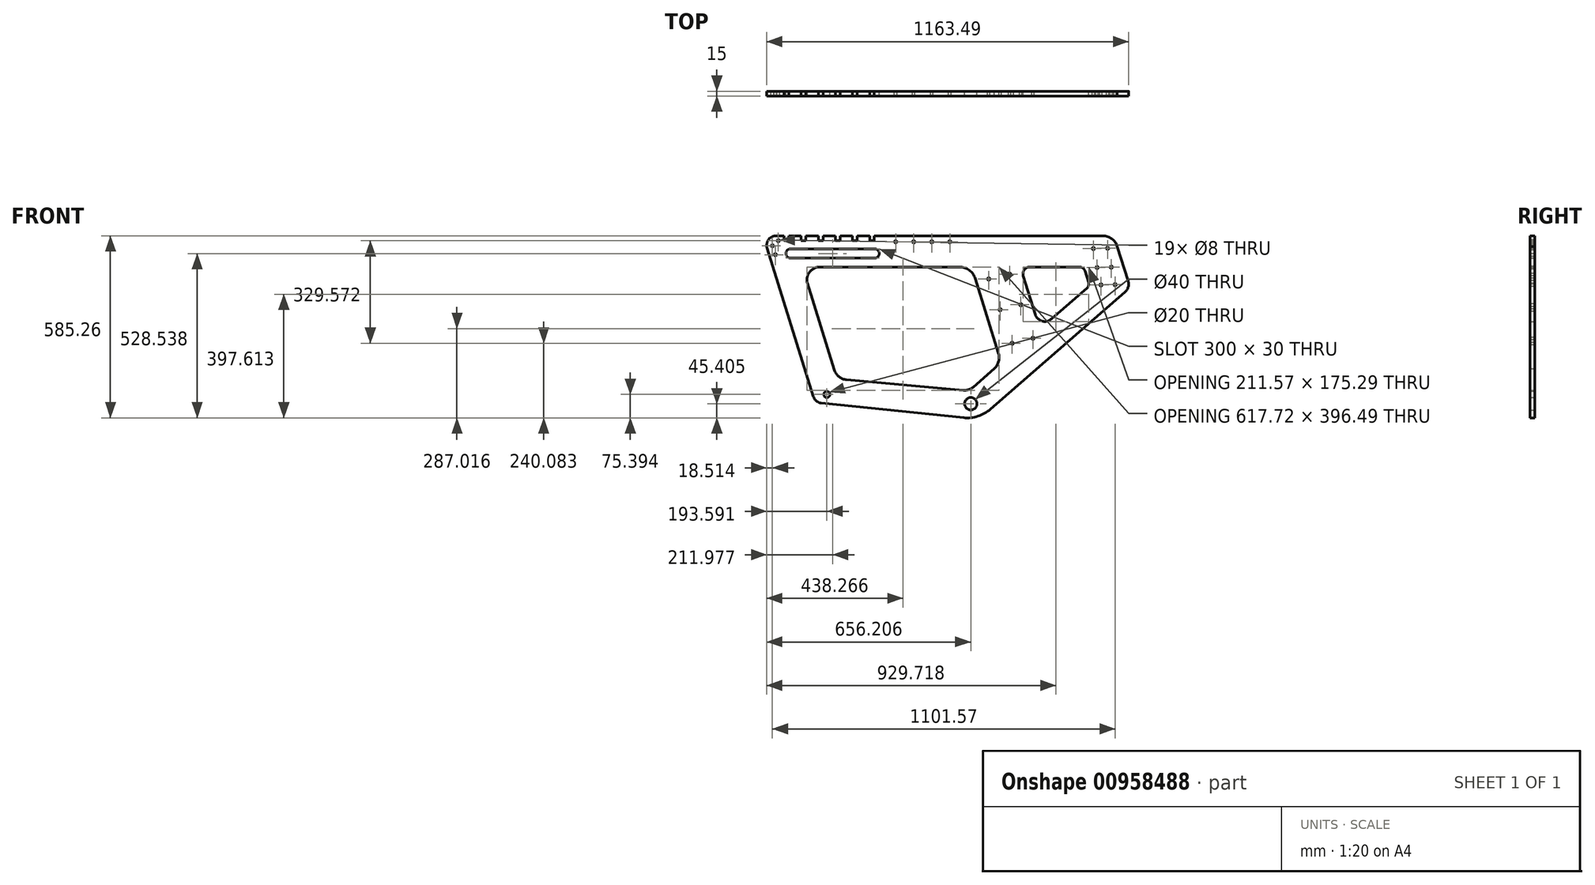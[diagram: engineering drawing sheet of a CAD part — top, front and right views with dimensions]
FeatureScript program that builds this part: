
annotation { "Feature Type Name" : "Feature", "Feature Type Description" : "" }
export const myFeature = defineFeature(function(context is Context, id is Id, definition is map)
    precondition{}
    {
        {
            var Q0;
            Q0=qCreatedBy(makeId("Front.planeOp"),FACE);
            var sketch = newSketch(context, id + "F0", { "sketchPlane" : qUnion([Q0])});
            skLineSegment(sketch, "E0", {"start": v(-250.21, -41.28) * mm, "end": v(207.37, -88.34) * mm});
            skLineSegment(sketch, "E1", {"start": v(-424.46, 456.77) * mm, "end": v(-275.56, -20.55) * mm});
            skLineSegment(sketch, "E2", {"start": v(293.18, -61.15) * mm, "end": v(726.16, 315.74) * mm});
            skArc(sketch, "E3", {"start": v(-275.56, -20.55) * mm, "mid": v(-266, -34.72) * mm, "end": v(-250.21, -41.28) * mm});
            skLineSegment(sketch, "E4", {"start": v(-295.43, 345.38) * mm, "end": v(-208.05, 65.27) * mm});
            skLineSegment(sketch, "E5", {"start": v(238.22, 10.33) * mm, "end": v(306.1, 69.42) * mm});
            skLineSegment(sketch, "E6", {"start": v(701.38, 462.39) * mm, "end": v(736.13, 350.96) * mm});
            skArc(sketch, "E7", {"start": v(207.37, -88.34) * mm, "mid": v(253.1, -83.65) * mm, "end": v(293.18, -61.15) * mm});
            skLineSegment(sketch, "E8", {"start": v(-254.58, 396.32) * mm, "end": v(193.57, 396.32) * mm});
            skLineSegment(sketch, "E9.bottom", {"start": v(-369.7, 496.32) * mm, "end": v(-354.7, 496.32) * mm});
            skLineSegment(sketch, "E9.top", {"start": v(-369.7, 481.32) * mm, "end": v(-354.7, 481.32) * mm});
            skLineSegment(sketch, "E9.left", {"start": v(-369.7, 496.32) * mm, "end": v(-369.7, 481.32) * mm});
            skLineSegment(sketch, "E9.right", {"start": v(-354.7, 496.32) * mm, "end": v(-354.7, 481.32) * mm});
            skLineSegment(sketch, "E10.bottom", {"start": v(-348.86, 454.6) * mm, "end": v(-78.86, 454.6) * mm});
            skLineSegment(sketch, "E10.top", {"start": v(-348.86, 424.6) * mm, "end": v(-78.86, 424.6) * mm});
            skArc(sketch, "E11", {"start": v(-78.86, 424.6) * mm, "mid": v(-63.86, 439.6) * mm, "end": v(-78.86, 454.6) * mm});
            skArc(sketch, "E12", {"start": v(-348.86, 454.6) * mm, "mid": v(-363.86, 439.6) * mm, "end": v(-348.86, 424.6) * mm});
            skLineSegment(sketch, "E13.bottom", {"start": v(-314.7, 496.32) * mm, "end": v(-299.7, 496.32) * mm});
            skLineSegment(sketch, "E13.top", {"start": v(-314.7, 481.32) * mm, "end": v(-299.7, 481.32) * mm});
            skLineSegment(sketch, "E13.left", {"start": v(-314.7, 496.32) * mm, "end": v(-314.7, 481.32) * mm});
            skLineSegment(sketch, "E13.right", {"start": v(-299.7, 496.32) * mm, "end": v(-299.7, 481.32) * mm});
            skLineSegment(sketch, "E14.bottom", {"start": v(-259.7, 496.32) * mm, "end": v(-244.7, 496.32) * mm});
            skLineSegment(sketch, "E14.top", {"start": v(-259.7, 481.32) * mm, "end": v(-244.7, 481.32) * mm});
            skLineSegment(sketch, "E14.left", {"start": v(-259.7, 496.32) * mm, "end": v(-259.7, 481.32) * mm});
            skLineSegment(sketch, "E14.right", {"start": v(-244.7, 496.32) * mm, "end": v(-244.7, 481.32) * mm});
            skLineSegment(sketch, "E15.bottom", {"start": v(-204.7, 496.32) * mm, "end": v(-189.7, 496.32) * mm});
            skLineSegment(sketch, "E15.top", {"start": v(-204.7, 481.32) * mm, "end": v(-189.7, 481.32) * mm});
            skLineSegment(sketch, "E15.left", {"start": v(-204.7, 496.32) * mm, "end": v(-204.7, 481.32) * mm});
            skLineSegment(sketch, "E15.right", {"start": v(-189.7, 496.32) * mm, "end": v(-189.7, 481.32) * mm});
            skLineSegment(sketch, "E16.bottom", {"start": v(-149.7, 496.32) * mm, "end": v(-134.7, 496.32) * mm});
            skLineSegment(sketch, "E16.top", {"start": v(-149.7, 481.32) * mm, "end": v(-134.7, 481.32) * mm});
            skLineSegment(sketch, "E16.left", {"start": v(-149.7, 496.32) * mm, "end": v(-149.7, 481.32) * mm});
            skLineSegment(sketch, "E16.right", {"start": v(-134.7, 496.32) * mm, "end": v(-134.7, 481.32) * mm});
            skLineSegment(sketch, "E17.bottom", {"start": v(-94.7, 496.32) * mm, "end": v(-79.7, 496.32) * mm});
            skLineSegment(sketch, "E17.top", {"start": v(-94.7, 481.32) * mm, "end": v(-79.7, 481.32) * mm});
            skLineSegment(sketch, "E17.left", {"start": v(-94.7, 496.32) * mm, "end": v(-94.7, 481.32) * mm});
            skLineSegment(sketch, "E17.right", {"start": v(-79.7, 496.32) * mm, "end": v(-79.7, 481.32) * mm});
            skCircle(sketch, "E18", {"center": v(-232.25, -13.55) * mm, "radius": 10 * mm});
            skCircle(sketch, "E19", {"center": v(230.37, -43.54) * mm, "radius": 20 * mm});
            skLineSegment(sketch, "E20", {"start": v(-395.36, 496.32) * mm, "end": v(654.64, 496.32) * mm});
            skArc(sketch, "E21", {"start": v(-395.36, 496.32) * mm, "mid": v(-419.91, 483.9) * mm, "end": v(-424.46, 456.77) * mm});
            skLineSegment(sketch, "E22", {"start": v(-552.23, 546.32) * mm, "end": v(-62.69, 546.32) * mm});
            skArc(sketch, "E23", {"start": v(701.38, 462.39) * mm, "mid": v(683.51, 486.94) * mm, "end": v(654.64, 496.32) * mm});
            skArc(sketch, "E24", {"start": v(726.16, 315.74) * mm, "mid": v(736.39, 331.87) * mm, "end": v(736.13, 350.96) * mm});
            skArc(sketch, "E25", {"start": v(-254.58, 396.32) * mm, "mid": v(-287.23, 380.65) * mm, "end": v(-295.43, 345.38) * mm});
            skLineSegment(sketch, "E26", {"start": v(-567.52, -105.42) * mm, "end": v(-102.94, -105.42) * mm});
            skLineSegment(sketch, "E27", {"start": v(-168.81, 33.6) * mm, "end": v(206.36, 0) * mm});
            skLineSegment(sketch, "E28", {"start": v(222.93, 583.17) * mm, "end": v(825.25, 583.17) * mm});
            skArc(sketch, "E29", {"start": v(206.36, 0) * mm, "mid": v(223.34, 1.91) * mm, "end": v(238.22, 10.33) * mm});
            skCircle(sketch, "E30", {"center": v(-388.36, 480.72) * mm, "radius": 4 * mm});
            skCircle(sketch, "E31", {"center": v(-407.33, 464.34) * mm, "radius": 4 * mm});
            skCircle(sketch, "E32", {"center": v(-397.9, 435.7) * mm, "radius": 4 * mm});
            skCircle(sketch, "E33", {"center": v(669.92, 456.51) * mm, "radius": 4 * mm});
            skLineSegment(sketch, "E34", {"start": v(319.04, 120.05) * mm, "end": v(244.57, 358.8) * mm});
            skArc(sketch, "E35", {"start": v(244.57, 358.8) * mm, "mid": v(225.22, 385.93) * mm, "end": v(193.57, 396.32) * mm});
            skArc(sketch, "E36", {"start": v(306.1, 69.42) * mm, "mid": v(319.75, 92.9) * mm, "end": v(319.04, 120.05) * mm});
            skLineSegment(sketch, "E37", {"start": v(399.06, 367.25) * mm, "end": v(437.65, 243.53) * mm});
            skLineSegment(sketch, "E38", {"start": v(489.3, 228.9) * mm, "end": v(603.86, 328.6) * mm});
            skLineSegment(sketch, "E39", {"start": v(420.44, 396.32) * mm, "end": v(579.8, 396.32) * mm});
            skLineSegment(sketch, "E40", {"start": v(597.35, 383.41) * mm, "end": v(608.9, 346.39) * mm});
            skArc(sketch, "E41", {"start": v(420.44, 396.32) * mm, "mid": v(402.4, 387.2) * mm, "end": v(399.06, 367.25) * mm});
            skArc(sketch, "E42", {"start": v(437.65, 243.53) * mm, "mid": v(459.52, 222.23) * mm, "end": v(489.3, 228.9) * mm});
            skArc(sketch, "E43", {"start": v(603.86, 328.6) * mm, "mid": v(609.02, 336.75) * mm, "end": v(608.9, 346.39) * mm});
            skArc(sketch, "E44", {"start": v(597.35, 383.41) * mm, "mid": v(590.7, 392.75) * mm, "end": v(579.8, 396.32) * mm});
            skArc(sketch, "E45", {"start": v(-208.05, 65.27) * mm, "mid": v(-193.24, 43.48) * mm, "end": v(-168.81, 33.6) * mm});
            skLineSegment(sketch, "E46", {"start": v(0, 677.8) * mm, "end": v(0, 575.53) * mm});
            skLineSegment(sketch, "E47", {"start": v(230.37, -138.1) * mm, "end": v(230.37, -238.52) * mm});
            skCircle(sketch, "E48", {"center": v(681.85, 395.48) * mm, "radius": 4 * mm});
            skCircle(sketch, "E49", {"center": v(694.24, 339.48) * mm, "radius": 4 * mm});
            skCircle(sketch, "E50", {"center": v(624.39, 455.46) * mm, "radius": 4 * mm});
            skCircle(sketch, "E51", {"center": v(636.32, 394.43) * mm, "radius": 4 * mm});
            skCircle(sketch, "E52", {"center": v(648.7, 338.44) * mm, "radius": 4 * mm});
            skCircle(sketch, "E53", {"center": v(-11.1, 477.32) * mm, "radius": 4 * mm});
            skCircle(sketch, "E54", {"center": v(46.9, 477.32) * mm, "radius": 4 * mm});
            skCircle(sketch, "E55", {"center": v(104.9, 477.32) * mm, "radius": 4 * mm});
            skCircle(sketch, "E56", {"center": v(162.9, 477.32) * mm, "radius": 4 * mm});
            skCircle(sketch, "E57", {"center": v(288.05, 357.6) * mm, "radius": 4 * mm});
            skCircle(sketch, "E58", {"center": v(354.84, 373.3) * mm, "radius": 4 * mm});
            skCircle(sketch, "E59", {"center": v(324.48, 258.92) * mm, "radius": 4 * mm});
            skCircle(sketch, "E60", {"center": v(391.26, 274.62) * mm, "radius": 4 * mm});
            skCircle(sketch, "E61", {"center": v(363.42, 151.14) * mm, "radius": 4 * mm});
            skCircle(sketch, "E62", {"center": v(430.2, 166.84) * mm, "radius": 4 * mm});
            skSolve(sketch);
        }
        {
            var Q0;
            Q0=makeQuery(id+"F0.imprint","IMPRINT",FACE,{"disambiguationData":[TD([[makeQuery(id+"F0.imprint","IMPRINT",EDGE,{"derivedFrom":sQuery(id+"F0.wireOp",EDGE,"E0")}),1.0]])]});
            extrude(context, id + "F1", {"entities" : qUnion([Q0]), "endBound" : BoundingType.SYMMETRIC, "depth" : 15 * mm, "offsetDistance" : 25 * mm});
        }
    });
